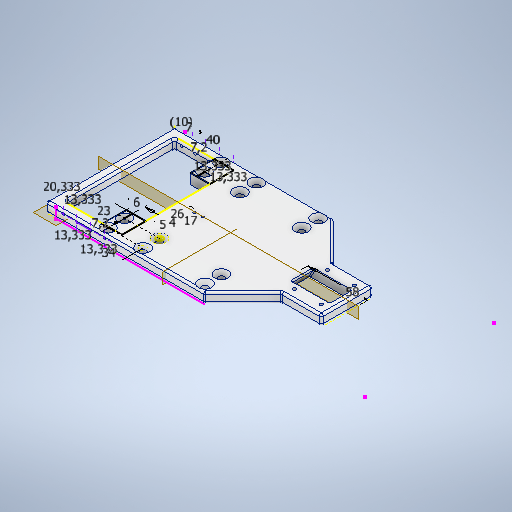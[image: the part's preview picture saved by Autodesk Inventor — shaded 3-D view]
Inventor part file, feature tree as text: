
AUTODESK INVENTOR PART (.ipt)
format: ipt  version: 2025 (Build 290162010, 162A)  size: 824,832 bytes
history: native  units: mm
features: sketch x15, hole x9, fillet x7, other x7, extrude x6, projected_geometry x5, plane x4, reference x4, chamfer x2, mirror x1, loft x1
ambient origin geometry x8: Origin, YZ Plane, XZ Plane, XY Plane, X Axis, Y Axis, Z Axis, Center Point
bodies: Volumenkörper1 (feature_tree)
feature tree (61):
  extrude  "main"  Depth=125.0mm
  hole  "BohrungLin"  [1 undecoded]
  plane  "Arbeitsebene4"
  extrude  "Extrusion7"  Depth=7.5mm
  fillet  "Rundung1"  Radius=77.0mm
  chamfer  "Fasen1"  Distance=3.5mm
  extrude  "Extrusion8"  Depth=10.0mm TaperAngle=45.0deg
  plane  "Arbeitsebene1"
  mirror  "Spiegeln1"
  plane  "Arbeitsebene2"
  hole  "Bohrung7"  [1 undecoded]
  loft  "Erhebung1"
  hole  "Bohrung10"  [1 undecoded]
  chamfer  "Fasen2"  Distance=5.0mm
  hole  "Bohrung11"  [1 undecoded]
  hole  "Bohrung12"  [1 undecoded]
  fillet  "Rundung5"  Radius=74.0mm
  fillet  "Rundung6"  Radius=16.0mm
  fillet  "Rundung7"  Radius=16.0mm
  fillet  "Rundung8"  Radius=70.0mm
  fillet  "Rundung9"  Radius=50.0mm
  plane  "Arbeitsebene5"
  extrude  "Extrusion11"  Depth=10.0mm
  hole  "SeildurchgangL"  [1 undecoded]
  hole  "SeildurchgangR"  [1 undecoded]
  fillet  "Rundung10"  Radius=16.0mm
  sketch  "Skizze29"  dims[d128=20.0mm d129=3.5mm d130=0.0mm]
  extrude  "Extrusion12"  Depth=10.0mm
  hole  "Bohrung13"  [1 undecoded]
  sketch  "Skizze30"  dims[d131=2.5mm d132=1.0mm d133=2.0mm d134=45.0deg d135=2.0mm d136=1.0mm d137=2.0mm d138=5.0mm d139=0.0mm d154=1.567mm d155=5.0mm d156=4.0mm d157=2.0mm d158=90.0deg d159=6.3mm d160=20.594885mm d208=0.0mm d209=90.0deg d210=0.0mm d211=90.0deg d220=74.0mm d221=16.0mm d222=16.0mm d223=70.0mm d224=50.0mm d225=16.0mm d226=16.0mm d227=16.0mm d228=16.0mm d229=41.95mm d230=6.779mm d231=8.0mm d232=2.459mm d233=6.0mm d234=13.0mm d235=2.0mm d236=90.0deg d237=11.8mm d238=20.594885mm d242=37.5mm d243=2.0mm d244=45.0deg d245=40.0mm d246=32.0mm d247=26.0mm d248=2.0mm d249=3.242mm d250=8.0mm d251=4.0mm d252=2.0mm d253=90.0deg d254=8.0mm d255=20.594885mm d257=22.0mm d259=14.0mm d261=2.0mm d264=30.0mm d265=20.0mm d266=1.567mm d267=5.0mm d268=6.3mm d269=2.0mm d270=90.0deg d271=6.3mm d272=20.594885mm d273=2.0mm d274=22.0mm d275=20.207259mm d276=14.871377mm d277=3.0mm d278=25.980762mm d279=17.550869mm d280=1.0mm d281=1.0mm d282=1.0mm d283=1.0mm d284=10.0mm d285=10.0mm d286=10.3335mm d287=53.332mm d288=10.334mm d289=10.334mm d290=0.0mm d291=0.0mm d292=13.333mm d293=13.333mm d294=13.333mm d295=13.333333mm d296=2.0mm d297=42.0mm d298=14.0mm d299=62.5mm d300=26.0mm d301=5.0mm d302=58.0mm d303=5.0mm d304=0.0mm d305=17.0mm d306=4.0mm d307=1.567mm d308=4.0mm d309=10.4mm d310=2.0mm d311=90.0deg d312=9.0mm d313=20.594885mm d315=23.0mm d318=0.0mm d319=0.0mm d320=6.0mm d321=34.0mm d322=6.4mm d323=6.0mm d324=12.6mm d325=2.0mm d326=90.0deg d327=8.0mm d328=20.594885mm]
  extrude  "Extrusion13"  Depth=10.0mm
  hole  "Bohrung14"  [1 undecoded]
  sketch  "Skizze1"  dims[d0=220.0mm d1=125.0mm]
  sketch  "Skizze2"  dims[d3=10.0mm d4=0.0mm d30=60.0mm]
  sketch  "Skizze4"  dims[d31=6.0mm d32=6.0mm d33=13.0mm d34=2.0mm d35=90.0deg d36=8.0mm d37=20.594885mm]
  sketch  "Skizze8"  dims[d50=2.459mm d51=1.0mm d52=4.0mm d53=2.0mm d54=90.0deg d55=1.0mm d56=20.594885mm]
  sketch  "Skizze12"  dims[d79=2.459mm d80=1.0mm d81=4.0mm d82=2.0mm d83=90.0deg d84=1.0mm d85=20.594885mm d88=7.5mm d89=77.0mm]
  projected_geometry  "Projizierte Kontur2"
  sketch  "Skizze13"  dims[d95=7.2mm]
  sketch  "Skizze15"  dims[d97=7.0mm]
  reference  "Referenz14"
  reference  "Referenz16"
  sketch  "Skizze22"  dims[d98=40.0mm]
  sketch  "Skizze23"  dims[d117=7.2mm]
  sketch  "Skizze25"  dims[d118=20.333333mm]
  sketch  "Skizze26"  dims[d120=13.333333mm]
  reference  "Referenz46"
  sketch  "Skizze27"  dims[d125=21.0mm]
  reference  "Referenz47"
  sketch  "Skizze28"  dims[d126=5.0mm]
  projected_geometry  "Projizierte Kontur3"
  projected_geometry  "Projizierte Kontur4"
  projected_geometry  "Projizierte Kontur5"
  projected_geometry  "Projizierte Kontur6"
  other  "<userpath>\GIT\HDVKBM\CAD\Krandemonstrator\Schlitten.iam"
  other  "Schlitten.iam"
  other  "DIN 7991 M6x16:2"
  other  "DIN 7991 M6x16:1"
  other  "Bedienhebel:1"
  other  "HebelhalterBlockBlind:1"
  other  "ISO 12633-2 - 20x20x2 - 200:1"
note: 9 required parameter values undecoded (feature->parameter linkage not recoverable at this tier; creation-order binding heuristic only, values carry confidence <= 0.55)
